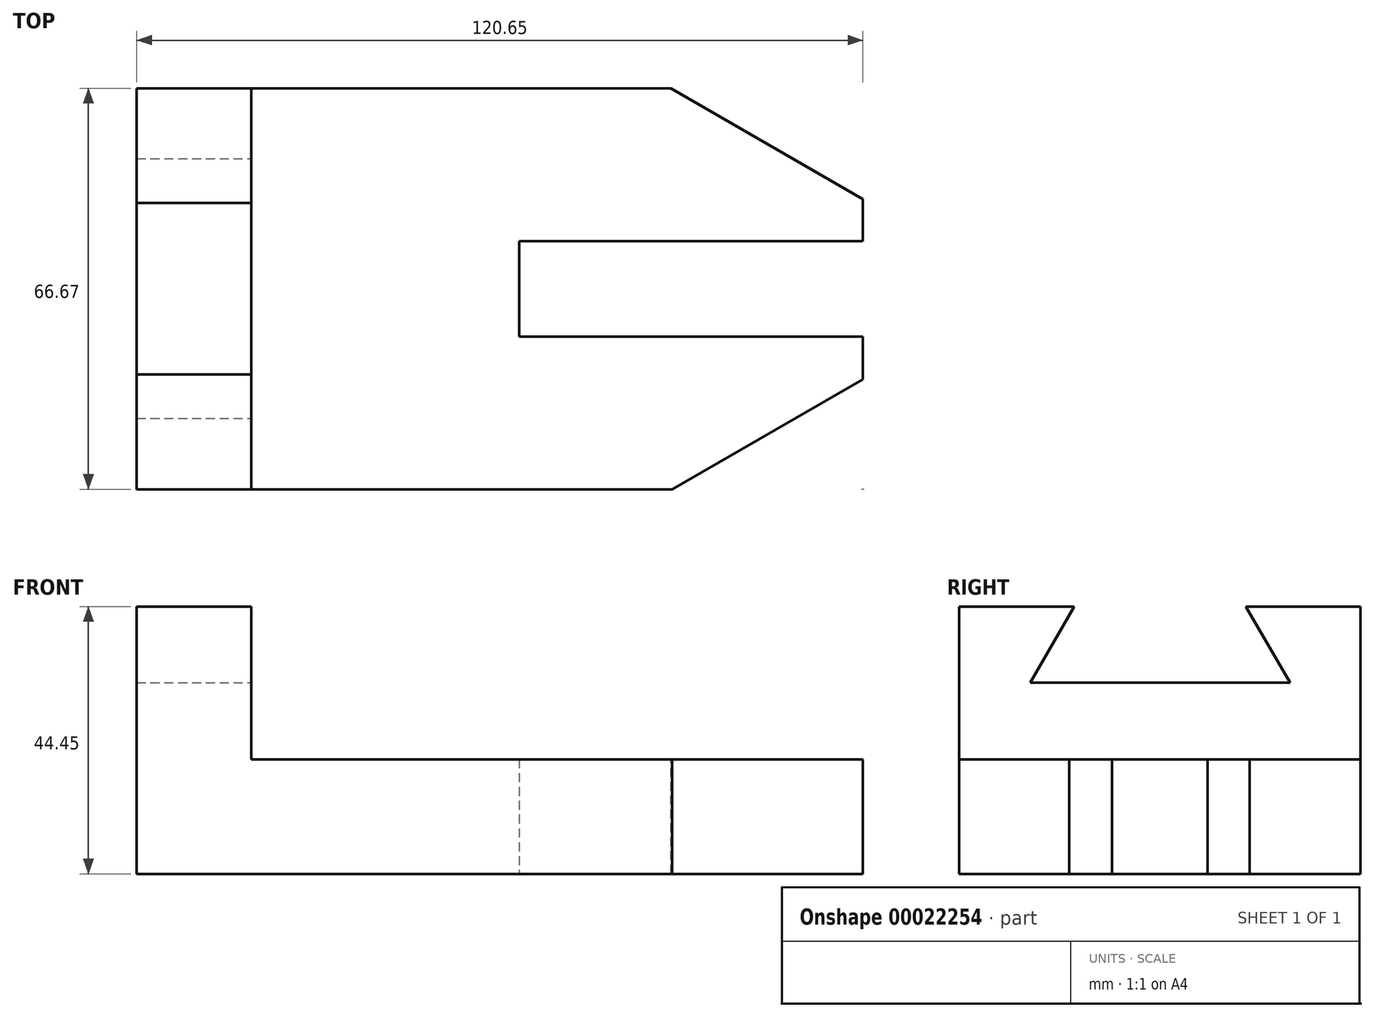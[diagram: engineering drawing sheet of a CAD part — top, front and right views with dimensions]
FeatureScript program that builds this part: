
annotation { "Feature Type Name" : "Feature", "Feature Type Description" : "" }
export const myFeature = defineFeature(function(context is Context, id is Id, definition is map)
    precondition{}
    {
        {
            var Q0;
            Q0=qCreatedBy(makeId("Front.planeOp"),FACE);
            var sketch = newSketch(context, id + "F0", { "sketchPlane" : qUnion([Q0])});
            skLineSegment(sketch, "E0.bottom", {"start": v(-43.96, 24.37) * mm, "end": v(-24.91, 24.37) * mm});
            skLineSegment(sketch, "E0.top", {"start": v(-43.96, -20.08) * mm, "end": v(-24.91, -20.08) * mm});
            skLineSegment(sketch, "E0.left", {"start": v(-43.96, 24.37) * mm, "end": v(-43.96, -20.08) * mm});
            skLineSegment(sketch, "E0.right", {"start": v(-24.91, 24.37) * mm, "end": v(-24.91, -20.08) * mm});
            skLineSegment(sketch, "E1.bottom", {"start": v(-43.96, -20.08) * mm, "end": v(76.69, -20.08) * mm});
            skLineSegment(sketch, "E1.top", {"start": v(-43.96, -1.03) * mm, "end": v(76.69, -1.03) * mm});
            skLineSegment(sketch, "E1.left", {"start": v(-43.96, -20.08) * mm, "end": v(-43.96, -1.03) * mm});
            skLineSegment(sketch, "E1.right", {"start": v(76.69, -20.08) * mm, "end": v(76.69, -1.03) * mm});
            skSolve(sketch);
        }
        {
            var Q0;
            Q0 = qSketchRegion(id + "F0", true);
            extrude(context, id + "F1", {"entities" : qUnion([Q0]), "depth" : 66.67 * mm});
        }
        {
            var Q0;
            Q0=qCreatedBy(makeId("Right.planeOp"),FACE);
            var sketch = newSketch(context, id + "F2", { "sketchPlane" : qUnion([Q0])});
            skLineSegment(sketch, "E2", {"start": v(0, 24.38) * mm, "end": v(-19.05, 24.38) * mm});
            skLineSegment(sketch, "E3.MirrorCS", {"start": v(-66.61, 24.41) * mm, "end": v(-47.56, 24.39) * mm});
            skLineSegment(sketch, "E4", {"start": v(0, 11.68) * mm, "end": v(-66.97, 11.68) * mm});
            skLineSegment(sketch, "E5", {"start": v(-19.05, 24.38) * mm, "end": v(-11.72, 11.68) * mm});
            skLineSegment(sketch, "E6", {"start": v(-47.56, 24.39) * mm, "end": v(-54.9, 11.68) * mm});
            skLineSegment(sketch, "E7", {"start": v(-19.05, 24.38) * mm, "end": v(-47.56, 24.39) * mm});
            skSolve(sketch);
        }
        {
            var Q0;
            Q0=qCreatedBy(makeId("Top.planeOp"),FACE);
            var sketch = newSketch(context, id + "F3", { "sketchPlane" : qUnion([Q0])});
            skLineSegment(sketch, "E8", {"start": v(19.55, -66.68) * mm, "end": v(19.55, -41.28) * mm});
            skLineSegment(sketch, "E9", {"start": v(19.55, -41.28) * mm, "end": v(19.55, -25.4) * mm});
            skLineSegment(sketch, "E10", {"start": v(19.55, -25.4) * mm, "end": v(19.55, 0) * mm});
            skLineSegment(sketch, "E11", {"start": v(19.55, -25.4) * mm, "end": v(76.7, -25.4) * mm});
            skLineSegment(sketch, "E12", {"start": v(19.55, -41.28) * mm, "end": v(76.7, -41.28) * mm});
            skLineSegment(sketch, "E13", {"start": v(76.7, -41.28) * mm, "end": v(76.7, -25.4) * mm});
            skLineSegment(sketch, "E14", {"start": v(76.69, -66.71) * mm, "end": v(44.94, -66.71) * mm});
            skLineSegment(sketch, "E15.MirrorCS", {"start": v(76.78, 0) * mm, "end": v(44.78, 0) * mm});
            skLineSegment(sketch, "E16", {"start": v(44.94, -66.71) * mm, "end": v(76.72, -48.36) * mm});
            skLineSegment(sketch, "E17", {"start": v(44.78, 0) * mm, "end": v(76.78, -18.48) * mm});
            skLineSegment(sketch, "E18", {"start": v(76.69, -66.71) * mm, "end": v(76.72, -48.36) * mm});
            skLineSegment(sketch, "E19", {"start": v(76.78, -18.48) * mm, "end": v(76.78, 0) * mm});
            skSolve(sketch);
        }
        {
            var Q0;
            Q0=sQuery(id+"F3.wireOp",EDGE,"E11");
            var Q1;
            Q1=sQuery(id+"F3.wireOp",EDGE,"E13");
            var Q2;
            Q2=sQuery(id+"F3.wireOp",EDGE,"E12");
            var Q3;
            Q3=sQuery(id+"F3.wireOp",EDGE,"E9");
            extrude(context, id + "F4", {"bodyType" : ToolBodyType.SURFACE, "surfaceEntities" : qUnion([Q0, Q1, Q2, Q3]), "oppositeDirection" : true, "depth" : 20.32 * mm});
        }
        {
            var Q0;
            Q0=makeQuery(id+"F4.opExtrude","SWEPT_FACE",FACE,{"disambiguationData":[OSD([sQuery(id+"F3.wireOp",EDGE,"E13")])]});
            extrude(context, id + "F5", {"entities" : qUnion([Q0]), "operationType" : NewBodyOperationType.REMOVE, "oppositeDirection" : true, "depth" : 57.15 * mm});
        }
        {
            var Q0;
            {var subQ1=sQuery(id+"F2.wireOp",EDGE,"E5");Q0=makeQuery(id+"F2.imprint","IMPRINT",FACE,{"disambiguationData":[TD([[makeQuery(id+"F2.imprint","IMPRINT",EDGE,{"derivedFrom":subQ1}),-1.0]])]});}
            extrude(context, id + "F6", {"entities" : qUnion([Q0]), "operationType" : NewBodyOperationType.REMOVE, "oppositeDirection" : true, "depth" : 44.45 * mm});
        }
        {
            var Q0;
            Q0=makeQuery(id+"F3.imprint","IMPRINT",FACE,{"disambiguationData":[TD([[makeQuery(id+"F3.imprint","IMPRINT",EDGE,{"derivedFrom":sQuery(id+"F3.wireOp",EDGE,"E14")}),-1.0]])]});
            extrude(context, id + "F7", {"entities" : qUnion([Q0]), "operationType" : NewBodyOperationType.REMOVE, "oppositeDirection" : true, "depth" : 20.32 * mm});
        }
        {
            var Q0;
            Q0=makeQuery(id+"F3.imprint","IMPRINT",FACE,{"disambiguationData":[TD([[makeQuery(id+"F3.imprint","IMPRINT",EDGE,{"derivedFrom":sQuery(id+"F3.wireOp",EDGE,"E15.MirrorCS")}),1.0]])]});
            extrude(context, id + "F8", {"entities" : qUnion([Q0]), "operationType" : NewBodyOperationType.REMOVE, "oppositeDirection" : true, "depth" : 20.32 * mm});
        }
    });
